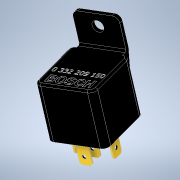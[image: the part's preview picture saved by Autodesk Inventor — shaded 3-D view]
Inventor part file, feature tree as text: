
AUTODESK INVENTOR PART (.ipt)
format: ipt  version: 2021 (Build 250183000, 183)  size: 794,624 bytes
history: native  units: mm
features: sketch x8, extrude x7, plane x1, pattern_linear x1, fillet x1, chamfer x1, emboss x1, projected_geometry x1
ambient origin geometry x8: Origin, YZ Plane, XZ Plane, XY Plane, X Axis, Y Axis, Z Axis, Center Point
bodies: Solid1 (feature_tree)
feature tree (21):
  extrude  "Extrusion1"  Depth=28.0mm
  plane  "Work Plane2"
  extrude  "Extrusion2"  Depth=3.0mm
  extrude  "Extrusion3"  Depth=22.0mm TaperAngle=0.0deg
  extrude  "Extrusion4"  Depth=5.5mm
  pattern_linear  "Rectangular Pattern1"  Spacing1=2.0mm  [1 undecoded]
  fillet  "Fillet1"  Radius=1.0mm
  extrude  "Extrusion5"  Depth=0.1mm
  chamfer  "Chamfer1"  Distance=2.0mm
  extrude  "Extrusion6"  Depth=0.1mm
  extrude  "Extrusion7"  Depth=0.1mm
  emboss  "Emboss1"
  sketch  "Sketch1"  dims[d0=28.0mm d1=28.0mm]
  sketch  "Sketch2"  dims[d3=26.9mm d4=0.0mm d5=3.0mm]
  sketch  "Sketch3"  dims[d6=1.0mm d13=22.0mm d14=0.0mm]
  sketch  "Sketch4"  dims[d15=-3.0mm d16=5.5mm]
  projected_geometry  "Projected Loop1"
  sketch  "Sketch5"  dims[d17=6.0mm]
  sketch  "Sketch6"  dims[d18=26.9mm d19=0.0mm]
  sketch  "Sketch7"  dims[d20=15.0mm]
  sketch  "Sketch8"  dims[d21=1.0mm d22=0.0mm d30=2.0mm d33=1.0mm d35=16.0mm d36=2.0mm d39=2.0mm d40=3.0mm d41=30.0mm d43=10.5mm d44=3.0mm d45=11.0mm d46=0.0mm d47=1.0mm d48=2.0mm d49=45.0deg d50=2.0mm d51=4.0mm d52=8.5mm d53=0.0mm d54=2.0mm d55=4.0mm d56=2.0mm d57=4.0mm d58=22.5mm d59=0.0mm d60=0.1mm d61=0.0mm]
note: 1 required parameter value undecoded (feature->parameter linkage not recoverable at this tier; creation-order binding heuristic only, values carry confidence <= 0.55)
